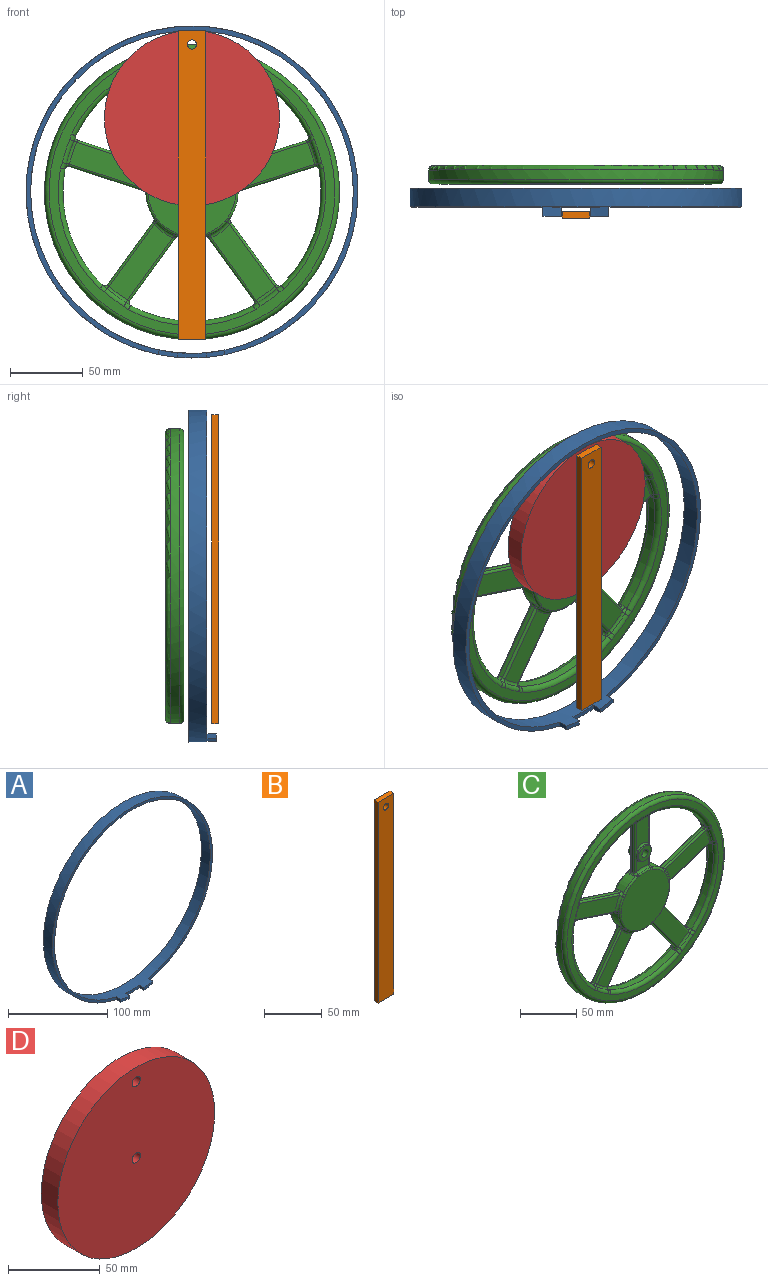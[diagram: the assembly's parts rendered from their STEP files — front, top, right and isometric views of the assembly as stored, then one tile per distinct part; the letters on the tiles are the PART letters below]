
ASSEMBLY  parts=4 mates=4
PART A: 11 faces, bbox 228.6x19.1x228.6 mm
  f0: plane 228.6x226.32mm, normal (0,-1,0), area 2103.2mm2, adj f2,f3,f6,f9
  f1: plane 20.07x3.63mm, normal (0,-1,0), area 63.8mm2, adj f2,f3,f5,f8
  f2: cylinder r=111.12mm len=222.25mm, axis (0,1,0), area 9030.5mm2, adj f0,f1,f4,f5,f6,f7,f8,f9
  f3: cylinder r=114.3mm len=228.6mm, axis (0,1,0), area 9283.8mm2, adj f0,f1,f4,f5,f6,f7,f8,f9
  f4: plane 228.6x228.6mm, normal (0,1,0), area 2248.5mm2, adj f2,f3
  f5: plane 6.35x3.19mm, normal (-1,0,0), area 20.2mm2, adj f1,f2,f3,f7
  f6: plane 6.35x3.24mm, normal (1,0,0), area 20.6mm2, adj f0,f2,f3,f7
  f7: plane 12.7x5.08mm, normal (0,-1,0), area 40.8mm2, adj f2,f3,f5,f6
  f8: plane 6.35x3.19mm, normal (1,0,0), area 20.2mm2, adj f1,f2,f3,f10
  f9: plane 6.35x3.24mm, normal (-1,0,0), area 20.6mm2, adj f0,f2,f3,f10
  f10: plane 12.7x5.08mm, normal (0,-1,0), area 40.8mm2, adj f2,f3,f8,f9
PART B: 7 faces, bbox 19.1x4.8x212.7 mm
  f0: plane 212.73x19.05mm, normal (0,-1,0), area 4020.7mm2, adj f1,f3,f4,f5,f6
  f1: plane 19.05x4.76mm, normal (0,0,-1), area 90.7mm2, adj f0,f2,f4,f5
  f2: plane 212.73x19.05mm, normal (0,1,0), area 4020.7mm2, adj f1,f3,f4,f5,f6
  f3: cylinder r=3.17mm len=6.35mm, axis (0,1,0), area 95mm2, adj f0,f2
  f4: plane 212.73x4.76mm, normal (1,0,0), area 1013.1mm2, adj f0,f1,f2,f6
  f5: plane 212.73x4.76mm, normal (-1,0,0), area 1013.1mm2, adj f0,f1,f2,f6
  f6: plane 19.05x4.76mm, normal (0,0,1), area 90.7mm2, adj f0,f2,f4,f5
PART C: 232 faces, bbox 219.9x12.7x219.9 mm
  f0: cylinder r=31.75mm len=19.11mm, axis (0,-1,0), area 174.7mm2, adj f72,f74,f76,f93,f95,f97,f205,f225
  f1: cylinder r=31.75mm len=20.1mm, axis (0,-1,0), area 174.7mm2, adj f96,f98,f100,f117,f119,f121,f197,f217
  f2: cylinder r=31.75mm len=19.11mm, axis (0,-1,0), area 174.7mm2, adj f120,f122,f124,f141,f143,f145,f192,f212
  f3: cylinder r=31.75mm len=16.26mm, axis (0,-1,0), area 174.7mm2, adj f33,f35,f37,f144,f146,f148,f200,f220
  f4: cylinder r=88.9mm len=80.24mm, axis (0,-1,0), area 554.9mm2, adj f113,f115,f116,f133,f134,f136,f166,f187
  f5: cylinder r=88.9mm len=84.37mm, axis (0,-1,0), area 554.9mm2, adj f89,f91,f92,f109,f110,f112,f158,f179
  f6: cylinder r=88.9mm len=80.24mm, axis (0,-1,0), area 554.9mm2, adj f65,f67,f68,f85,f86,f88,f150,f171
  f7: cylinder r=88.9mm len=68.25mm, axis (0,-1,0), area 554.9mm2, adj f29,f31,f32,f61,f62,f64,f155,f176
  f8: plane 15.88x12.36mm, normal (0,1,0), area 138.7mm2, adj f21,f22,f39,f46
  f9: plane 30.47x15.88mm, normal (0,-1,0), area 434.2mm2, adj f23,f24,f27,f51
  f10: plane 196.85x196.85mm, normal (0,1,0), area 3854.4mm2, adj f149,f150,f151,f152,f153,f154,f155,f156
  f11: cylinder r=101.6mm len=203.2mm, axis (0,-1,0), area 4053.7mm2, adj f169,f190
  f12: cylinder r=88.9mm len=68.25mm, axis (0,-1,0), area 554.9mm2, adj f25,f26,f28,f137,f139,f140,f163,f184
  f13: plane 196.85x196.85mm, normal (0,-1,0), area 3854.4mm2, adj f170,f171,f172,f173,f174,f175,f176,f177
  f14: plane 30.47x15.88mm, normal (0,1,0), area 434.2mm2, adj f21,f22,f30,f47
  f15: plane 53.74x3.18mm, normal (1,0,0), area 170.6mm2, adj f21,f24,f26,f35
  f16: plane 53.74x3.18mm, normal (-1,0,0), area 170.6mm2, adj f22,f23,f31,f38
  f17: plane 15.88x12.36mm, normal (0,-1,0), area 138.7mm2, adj f23,f24,f34,f50
  f18: plane 60.4x60.35mm, normal (0,1,0), area 2864.4mm2, adj f191,f192,f193,f194,f195,f196,f197,f198
  f19: plane 60.4x60.35mm, normal (0,-1,0), area 2864.4mm2, adj f211,f212,f213,f214,f215,f216,f217,f218
  f20: cylinder r=31.75mm len=16.26mm, axis (0,-1,0), area 174.7mm2, adj f36,f38,f40,f69,f71,f73,f208,f228
  f21: cylinder r=1.59mm len=54.2mm, axis (0,0,1), area 127.2mm2, adj f8,f14,f15,f28,f37,f45
  f22: cylinder r=1.59mm len=54.2mm, axis (0,0,-1), area 127.2mm2, adj f8,f14,f16,f32,f40,f48
  f23: cylinder r=1.59mm len=54.2mm, axis (0,0,-1), area 127.2mm2, adj f9,f16,f17,f29,f36,f49
  f24: cylinder r=1.59mm len=54.2mm, axis (0,0,1), area 127.2mm2, adj f9,f15,f17,f25,f33,f52
  f25: bspline ~4.96x4.83mm, area 11.7mm2, adj f12,f24,f26,f27,f182
  f26: cylinder r=2.36mm len=3.18mm, axis (0,-1,0), area 12.8mm2, adj f12,f15,f25,f28
  f27: torus R=86.54mm, axis (0,-1,0), area 43mm2, adj f9,f25,f29,f180
  f28: bspline ~4.96x4.83mm, area 11.7mm2, adj f12,f21,f26,f30,f161
  f29: bspline ~4.96x4.83mm, area 11.7mm2, adj f7,f23,f27,f31,f178
  f30: torus R=86.54mm, axis (0,1,0), area 43mm2, adj f14,f28,f32,f159
  f31: cylinder r=2.36mm len=3.18mm, axis (0,-1,0), area 12.8mm2, adj f7,f16,f29,f32
  f32: bspline ~4.96x4.83mm, area 11.7mm2, adj f7,f22,f30,f31,f157
  f33: bspline ~4.79x4.5mm, area 12.4mm2, adj f3,f24,f34,f35,f222
  f34: torus R=34.11mm, axis (0,-1,0), area 49.9mm2, adj f17,f33,f36,f224
  f35: cylinder r=2.36mm len=3.18mm, axis (0,-1,0), area 9.1mm2, adj f3,f15,f33,f37
  f36: bspline ~4.79x3.88mm, area 12.4mm2, adj f20,f23,f34,f38,f226
  f37: bspline ~4.79x4.5mm, area 12.4mm2, adj f3,f21,f35,f39,f202
  f38: cylinder r=2.36mm len=3.18mm, axis (0,-1,0), area 9.1mm2, adj f16,f20,f36,f40
  f39: torus R=34.11mm, axis (0,1,0), area 49.9mm2, adj f8,f37,f40,f204
  f40: bspline ~4.5x4.16mm, area 12.4mm2, adj f20,f22,f38,f39,f206
  f41: plane 15.88x15.88mm, normal (0,-1,0), area 148.4mm2, adj f42,f231
  f42: cylinder r=7.94mm len=15.88mm, axis (0,-1,0), area 79.2mm2, adj f41,f49,f50,f51,f52
  f43: cylinder r=7.94mm len=15.88mm, axis (0,-1,0), area 79.2mm2, adj f44,f45,f46,f47,f48
  f44: plane 15.88x15.88mm, normal (0,1,0), area 148.4mm2, adj f43,f231
  f45: bspline ~12.24x2.65mm, area 19.1mm2, adj f21,f43,f46,f47
  f46: torus R=9.53mm, axis (0,1,0), area 41.8mm2, adj f8,f43,f45,f48
  f47: torus R=9.53mm, axis (0,1,0), area 41.8mm2, adj f14,f43,f45,f48
  f48: bspline ~12.24x2.65mm, area 19.1mm2, adj f22,f43,f46,f47
  f49: bspline ~12.24x2.65mm, area 19.1mm2, adj f23,f42,f50,f51
  f50: torus R=9.53mm, axis (0,-1,0), area 41.8mm2, adj f17,f42,f49,f52
  f51: torus R=9.53mm, axis (0,-1,0), area 41.8mm2, adj f9,f42,f49,f52
  f52: bspline ~12.24x2.65mm, area 19.1mm2, adj f24,f42,f50,f51
  f53: plane 55.31x31.48mm, normal (0,1,0), area 835.3mm2, adj f57,f58,f66,f75
  f54: plane 51.11x16.61mm, normal (0.31,0,0.95), area 170.6mm2, adj f57,f60,f62,f71
  f55: plane 51.11x16.61mm, normal (-0.31,0,-0.95), area 170.6mm2, adj f58,f59,f67,f74
  f56: plane 55.31x31.48mm, normal (0,-1,0), area 835.3mm2, adj f59,f60,f63,f70
  f57: cylinder r=1.59mm len=52.04mm, axis (-0.95,0,0.31), area 133.1mm2, adj f53,f54,f64,f73
  f58: cylinder r=1.59mm len=52.04mm, axis (0.95,0,-0.31), area 133.1mm2, adj f53,f55,f68,f76
  f59: cylinder r=1.59mm len=52.04mm, axis (0.95,0,-0.31), area 133.1mm2, adj f55,f56,f65,f72
  f60: cylinder r=1.59mm len=52.04mm, axis (-0.95,0,0.31), area 133.1mm2, adj f54,f56,f61,f69
  f61: bspline ~4.96x4.17mm, area 11.7mm2, adj f7,f60,f62,f63,f174
  f62: cylinder r=2.36mm len=3.28mm, axis (0,-1,0), area 12.8mm2, adj f7,f54,f61,f64
  f63: torus R=86.54mm, axis (0,-1,0), area 43mm2, adj f56,f61,f65,f172
  f64: bspline ~4.96x4.83mm, area 11.7mm2, adj f7,f57,f62,f66,f153
  f65: bspline ~4.89x4.17mm, area 11.7mm2, adj f6,f59,f63,f67,f170
  f66: torus R=86.54mm, axis (0,1,0), area 43mm2, adj f53,f64,f68,f151
  f67: cylinder r=2.36mm len=3.18mm, axis (0,-1,0), area 12.8mm2, adj f6,f55,f65,f68
  f68: bspline ~4.89x4.83mm, area 11.7mm2, adj f6,f58,f66,f67,f149
  f69: bspline ~4.79x4.51mm, area 12.4mm2, adj f20,f60,f70,f71,f230
  f70: torus R=34.11mm, axis (0,-1,0), area 49.9mm2, adj f56,f69,f72,f229
  f71: cylinder r=2.36mm len=3.18mm, axis (0,-1,0), area 9.1mm2, adj f20,f54,f69,f73
  f72: bspline ~4.79x4.68mm, area 12.4mm2, adj f0,f59,f70,f74,f227
  f73: bspline ~4.79x4.51mm, area 12.4mm2, adj f20,f57,f71,f75,f210
  f74: cylinder r=2.36mm len=3.18mm, axis (0,-1,0), area 9.1mm2, adj f0,f55,f72,f76
  f75: torus R=34.11mm, axis (0,1,0), area 49.9mm2, adj f53,f73,f76,f209
  f76: bspline ~4.68x4.16mm, area 12.4mm2, adj f0,f58,f74,f75,f207
  f77: plane 52.21x43.99mm, normal (0,1,0), area 835.3mm2, adj f81,f82,f90,f99
  f78: plane 43.48x31.59mm, normal (-0.81,0,0.59), area 170.6mm2, adj f81,f84,f86,f95
  f79: plane 43.48x31.59mm, normal (0.81,0,-0.59), area 170.6mm2, adj f82,f83,f91,f98
  f80: plane 52.21x43.99mm, normal (0,-1,0), area 835.3mm2, adj f83,f84,f87,f94
  f81: cylinder r=1.59mm len=44.78mm, axis (-0.59,0,-0.81), area 133.1mm2, adj f77,f78,f88,f97
  f82: cylinder r=1.59mm len=44.78mm, axis (0.59,0,0.81), area 133.1mm2, adj f77,f79,f92,f100
  f83: cylinder r=1.59mm len=44.78mm, axis (0.59,0,0.81), area 133.1mm2, adj f79,f80,f89,f96
  f84: cylinder r=1.59mm len=44.78mm, axis (-0.59,0,-0.81), area 133.1mm2, adj f78,f80,f85,f93
  f85: bspline ~4.83x4.81mm, area 11.7mm2, adj f6,f84,f86,f87,f173
  f86: cylinder r=2.36mm len=3.55mm, axis (0,-1,0), area 12.8mm2, adj f6,f78,f85,f88
  f87: torus R=86.54mm, axis (0,-1,0), area 43mm2, adj f80,f85,f89,f175
  f88: bspline ~4.83x4.81mm, area 11.7mm2, adj f6,f81,f86,f90,f152
  f89: bspline ~4.83x4.34mm, area 11.7mm2, adj f5,f83,f87,f91,f177
  f90: torus R=86.54mm, axis (0,1,0), area 43mm2, adj f77,f88,f92,f154
  f91: cylinder r=2.36mm len=3.47mm, axis (0,-1,0), area 12.8mm2, adj f5,f79,f89,f92
  f92: bspline ~4.83x4.34mm, area 11.7mm2, adj f5,f82,f90,f91,f156
  f93: bspline ~4.97x4.79mm, area 12.4mm2, adj f0,f84,f94,f95,f223
  f94: torus R=34.11mm, axis (0,-1,0), area 49.9mm2, adj f80,f93,f96,f221
  f95: cylinder r=2.36mm len=3.18mm, axis (0,-1,0), area 9.1mm2, adj f0,f78,f93,f97
  f96: bspline ~4.94x4.16mm, area 12.4mm2, adj f1,f83,f94,f98,f219
  f97: bspline ~4.79x4.7mm, area 12.4mm2, adj f0,f81,f95,f99,f203
  f98: cylinder r=2.36mm len=3.18mm, axis (0,-1,0), area 9.1mm2, adj f1,f79,f96,f100
  f99: torus R=34.11mm, axis (0,1,0), area 49.9mm2, adj f77,f97,f100,f201
  f100: bspline ~4.94x4.16mm, area 12.4mm2, adj f1,f82,f98,f99,f199
  f101: plane 52.21x43.99mm, normal (0,1,0), area 835.3mm2, adj f105,f106,f114,f123
  f102: plane 43.48x31.59mm, normal (-0.81,0,-0.59), area 170.6mm2, adj f105,f108,f110,f119
  f103: plane 43.48x31.59mm, normal (0.81,0,0.59), area 170.6mm2, adj f106,f107,f115,f122
  f104: plane 52.21x43.99mm, normal (0,-1,0), area 835.3mm2, adj f107,f108,f111,f118
  f105: cylinder r=1.59mm len=44.78mm, axis (0.59,0,-0.81), area 133.1mm2, adj f101,f102,f112,f121
  f106: cylinder r=1.59mm len=44.78mm, axis (-0.59,0,0.81), area 133.1mm2, adj f101,f103,f116,f124
  f107: cylinder r=1.59mm len=44.78mm, axis (-0.59,0,0.81), area 133.1mm2, adj f103,f104,f113,f120
  f108: cylinder r=1.59mm len=44.78mm, axis (0.59,0,-0.81), area 133.1mm2, adj f102,f104,f109,f117
  f109: bspline ~4.83x4.34mm, area 11.7mm2, adj f5,f108,f110,f111,f181
  f110: cylinder r=2.36mm len=3.47mm, axis (0,-1,0), area 12.8mm2, adj f5,f102,f109,f112
  f111: torus R=86.54mm, axis (0,-1,0), area 43mm2, adj f104,f109,f113,f183
  f112: bspline ~4.83x4.34mm, area 11.7mm2, adj f5,f105,f110,f114,f160
  f113: bspline ~4.83x4.81mm, area 11.7mm2, adj f4,f107,f111,f115,f185
  f114: torus R=86.54mm, axis (0,1,0), area 43mm2, adj f101,f112,f116,f162
  f115: cylinder r=2.36mm len=3.55mm, axis (0,-1,0), area 12.8mm2, adj f4,f103,f113,f116
  f116: bspline ~4.83x4.81mm, area 11.7mm2, adj f4,f106,f114,f115,f164
  f117: bspline ~4.94x4.79mm, area 12.4mm2, adj f1,f108,f118,f119,f215
  f118: torus R=34.11mm, axis (0,-1,0), area 49.9mm2, adj f104,f117,f120,f213
  f119: cylinder r=2.36mm len=3.18mm, axis (0,-1,0), area 9.1mm2, adj f1,f102,f117,f121
  f120: bspline ~4.97x4.16mm, area 12.4mm2, adj f2,f107,f118,f122,f211
  f121: bspline ~4.79x4.64mm, area 12.4mm2, adj f1,f105,f119,f123,f195
  f122: cylinder r=2.36mm len=3.18mm, axis (0,-1,0), area 9.1mm2, adj f2,f103,f120,f124
  f123: torus R=34.11mm, axis (0,1,0), area 49.9mm2, adj f101,f121,f124,f193
  f124: bspline ~4.97x4.79mm, area 12.4mm2, adj f2,f106,f122,f123,f191
  f125: plane 55.31x31.48mm, normal (0,1,0), area 835.3mm2, adj f129,f130,f138,f147
  f126: plane 51.11x16.61mm, normal (0.31,0,-0.95), area 170.6mm2, adj f129,f132,f134,f143
  f127: plane 51.11x16.61mm, normal (-0.31,0,0.95), area 170.6mm2, adj f130,f131,f139,f146
  f128: plane 55.31x31.48mm, normal (0,-1,0), area 835.3mm2, adj f131,f132,f135,f142
  f129: cylinder r=1.59mm len=52.04mm, axis (0.95,0,0.31), area 133.1mm2, adj f125,f126,f136,f145
  f130: cylinder r=1.59mm len=52.04mm, axis (-0.95,0,-0.31), area 133.1mm2, adj f125,f127,f140,f148
  f131: cylinder r=1.59mm len=52.04mm, axis (-0.95,0,-0.31), area 133.1mm2, adj f127,f128,f137,f144
  f132: cylinder r=1.59mm len=52.04mm, axis (0.95,0,0.31), area 133.1mm2, adj f126,f128,f133,f141
  f133: bspline ~4.89x4.83mm, area 11.7mm2, adj f4,f132,f134,f135,f189
  f134: cylinder r=2.36mm len=3.18mm, axis (0,-1,0), area 12.8mm2, adj f4,f126,f133,f136
  f135: torus R=86.54mm, axis (0,-1,0), area 43mm2, adj f128,f133,f137,f188
  f136: bspline ~4.89x4.83mm, area 11.7mm2, adj f4,f129,f134,f138,f168
  f137: bspline ~4.96x4.83mm, area 11.7mm2, adj f12,f131,f135,f139,f186
  f138: torus R=86.54mm, axis (0,1,0), area 43mm2, adj f125,f136,f140,f167
  f139: cylinder r=2.36mm len=3.28mm, axis (0,-1,0), area 12.8mm2, adj f12,f127,f137,f140
  f140: bspline ~4.96x4.17mm, area 11.7mm2, adj f12,f130,f138,f139,f165
  f141: bspline ~4.79x4.68mm, area 12.4mm2, adj f2,f132,f142,f143,f214
  f142: torus R=34.11mm, axis (0,-1,0), area 49.9mm2, adj f128,f141,f144,f216
  f143: cylinder r=2.36mm len=3.18mm, axis (0,-1,0), area 9.1mm2, adj f2,f126,f141,f145
  f144: bspline ~4.79x4.51mm, area 12.4mm2, adj f3,f131,f142,f146,f218
  f145: bspline ~4.79x4.68mm, area 12.4mm2, adj f2,f129,f143,f147,f194
  f146: cylinder r=2.36mm len=3.18mm, axis (0,-1,0), area 9.1mm2, adj f3,f127,f144,f148
  f147: torus R=34.11mm, axis (0,1,0), area 49.9mm2, adj f125,f145,f148,f196
  f148: bspline ~4.51x4.16mm, area 12.4mm2, adj f3,f130,f146,f147,f198
  f149: bspline ~5.07x4.22mm, area 15.8mm2, adj f10,f68,f150,f151
  f150: torus R=92.08mm, axis (0,1,0), area 444.1mm2, adj f6,f10,f149,f152
  f151: torus R=91.55mm, axis (0,1,0), area 59.3mm2, adj f10,f66,f149,f153
  f152: bspline ~5.76x4.91mm, area 15.8mm2, adj f10,f88,f150,f154
  f153: bspline ~6.52x4.64mm, area 15.8mm2, adj f10,f64,f151,f155
  f154: torus R=91.55mm, axis (0,1,0), area 59.3mm2, adj f10,f90,f152,f156
  f155: torus R=92.08mm, axis (0,1,0), area 444.1mm2, adj f7,f10,f153,f157
  f156: bspline ~5.54x5.47mm, area 15.8mm2, adj f10,f92,f154,f158
  f157: bspline ~5.84x3.57mm, area 15.8mm2, adj f10,f32,f155,f159
  f158: torus R=92.08mm, axis (0,1,0), area 444.1mm2, adj f5,f10,f156,f160
  f159: torus R=91.55mm, axis (0,1,0), area 59.3mm2, adj f10,f30,f157,f161
  f160: bspline ~5.27x5.09mm, area 15.8mm2, adj f10,f112,f158,f162
  f161: bspline ~6.02x3.57mm, area 15.8mm2, adj f10,f28,f159,f163
  f162: torus R=91.55mm, axis (0,1,0), area 59.3mm2, adj f10,f114,f160,f164
  f163: torus R=92.08mm, axis (0,1,0), area 444.1mm2, adj f10,f12,f161,f165
  f164: bspline ~6.04x5.17mm, area 15.8mm2, adj f10,f116,f162,f166
  f165: bspline ~6.36x4.59mm, area 15.8mm2, adj f10,f140,f163,f167
  f166: torus R=92.08mm, axis (0,1,0), area 444.1mm2, adj f4,f10,f164,f168
  f167: torus R=91.55mm, axis (0,1,0), area 59.3mm2, adj f10,f138,f165,f168
  f168: bspline ~5.34x4.32mm, area 15.8mm2, adj f10,f136,f166,f167
  f169: torus R=98.42mm, axis (0,1,0), area 3147.6mm2, adj f10,f11
  f170: bspline ~5.07x4.22mm, area 15.8mm2, adj f13,f65,f171,f172
  f171: torus R=92.08mm, axis (0,-1,0), area 444.1mm2, adj f6,f13,f170,f173
  f172: torus R=91.55mm, axis (0,-1,0), area 59.3mm2, adj f13,f63,f170,f174
  f173: bspline ~6.39x5.37mm, area 15.8mm2, adj f13,f85,f171,f175
  f174: bspline ~6.52x4.64mm, area 15.8mm2, adj f13,f61,f172,f176
  f175: torus R=91.55mm, axis (0,-1,0), area 59.3mm2, adj f13,f87,f173,f177
  f176: torus R=92.08mm, axis (0,-1,0), area 444.1mm2, adj f7,f13,f174,f178
  f177: bspline ~5.54x5.47mm, area 15.8mm2, adj f13,f89,f175,f179
  f178: bspline ~5.84x3.57mm, area 15.8mm2, adj f13,f29,f176,f180
  f179: torus R=92.08mm, axis (0,-1,0), area 444.1mm2, adj f5,f13,f177,f181
  f180: torus R=91.55mm, axis (0,-1,0), area 59.3mm2, adj f13,f27,f178,f182
  f181: bspline ~5.63x5.57mm, area 15.8mm2, adj f13,f109,f179,f183
  f182: bspline ~6.02x3.57mm, area 15.8mm2, adj f13,f25,f180,f184
  f183: torus R=91.55mm, axis (0,-1,0), area 59.3mm2, adj f13,f111,f181,f185
  f184: torus R=92.08mm, axis (0,-1,0), area 444.1mm2, adj f12,f13,f182,f186
  f185: bspline ~6.04x5.17mm, area 15.8mm2, adj f13,f113,f183,f187
  f186: bspline ~6.36x4.59mm, area 15.8mm2, adj f13,f137,f184,f188
  f187: torus R=92.08mm, axis (0,-1,0), area 444.1mm2, adj f4,f13,f185,f189
  f188: torus R=91.55mm, axis (0,-1,0), area 59.3mm2, adj f13,f135,f186,f189
  f189: bspline ~5.34x4.32mm, area 15.8mm2, adj f13,f133,f187,f188
  f190: torus R=98.42mm, axis (0,-1,0), area 3147.6mm2, adj f11,f13
  f191: bspline ~3.84x3.45mm, area 5.1mm2, adj f18,f124,f192,f193
  f192: torus R=30.16mm, axis (0,1,0), area 50.1mm2, adj f2,f18,f191,f194
  f193: torus R=30.24mm, axis (0,-1,0), area 31.9mm2, adj f18,f123,f191,f195
  f194: bspline ~3.5x1.81mm, area 5.1mm2, adj f18,f145,f192,f196
  f195: bspline ~3.78x2.7mm, area 5.1mm2, adj f18,f121,f193,f197
  f196: torus R=30.24mm, axis (0,-1,0), area 31.9mm2, adj f18,f147,f194,f198
  f197: torus R=30.16mm, axis (0,1,0), area 50.1mm2, adj f1,f18,f195,f199
  f198: bspline ~3.79x3.34mm, area 5.1mm2, adj f18,f148,f196,f200
  f199: bspline ~3.97x2.78mm, area 5.1mm2, adj f18,f100,f197,f201
  f200: torus R=30.16mm, axis (0,1,0), area 50.1mm2, adj f3,f18,f198,f202
  f201: torus R=30.24mm, axis (0,-1,0), area 31.9mm2, adj f18,f99,f199,f203
  f202: bspline ~3.58x2.47mm, area 5.1mm2, adj f18,f37,f200,f204
  f203: bspline ~3.69x3.33mm, area 5.1mm2, adj f18,f97,f201,f205
  f204: torus R=30.24mm, axis (0,-1,0), area 31.9mm2, adj f18,f39,f202,f206
  f205: torus R=30.16mm, axis (0,1,0), area 50.1mm2, adj f0,f18,f203,f207
  f206: bspline ~3.76x2.51mm, area 5.1mm2, adj f18,f40,f204,f208
  f207: bspline ~3.71x1.83mm, area 5.1mm2, adj f18,f76,f205,f209
  f208: torus R=30.16mm, axis (0,1,0), area 50.1mm2, adj f18,f20,f206,f210
  f209: torus R=30.24mm, axis (0,-1,0), area 31.9mm2, adj f18,f75,f207,f210
  f210: bspline ~3.63x3.24mm, area 5.1mm2, adj f18,f73,f208,f209
  f211: bspline ~4.33x3.89mm, area 5.1mm2, adj f19,f120,f212,f213
  f212: torus R=30.16mm, axis (0,-1,0), area 50.1mm2, adj f2,f19,f211,f214
  f213: torus R=30.24mm, axis (0,1,0), area 31.9mm2, adj f19,f118,f211,f215
  f214: bspline ~4.16x1.99mm, area 5.1mm2, adj f19,f141,f212,f216
  f215: bspline ~4.38x3.02mm, area 5.1mm2, adj f19,f117,f213,f217
  f216: torus R=30.24mm, axis (0,1,0), area 31.9mm2, adj f19,f142,f214,f218
  f217: torus R=30.16mm, axis (0,-1,0), area 50.1mm2, adj f1,f19,f215,f219
  f218: bspline ~3.86x3.39mm, area 5.1mm2, adj f19,f144,f216,f220
  f219: bspline ~4.57x3.1mm, area 5.1mm2, adj f19,f96,f217,f221
  f220: torus R=30.16mm, axis (0,-1,0), area 50.1mm2, adj f3,f19,f218,f222
  f221: torus R=30.24mm, axis (0,1,0), area 31.9mm2, adj f19,f94,f219,f223
  f222: bspline ~4.09x2.6mm, area 5.1mm2, adj f19,f33,f220,f224
  f223: bspline ~4.18x3.76mm, area 5.1mm2, adj f19,f93,f221,f225
  f224: torus R=30.24mm, axis (0,1,0), area 31.9mm2, adj f19,f34,f222,f226
  f225: torus R=30.16mm, axis (0,-1,0), area 50.1mm2, adj f0,f19,f223,f227
  f226: bspline ~4.27x2.64mm, area 5.1mm2, adj f19,f36,f224,f228
  f227: bspline ~4.37x2.01mm, area 5.1mm2, adj f19,f72,f225,f229
  f228: torus R=30.16mm, axis (0,-1,0), area 50.1mm2, adj f19,f20,f226,f230
  f229: torus R=30.24mm, axis (0,1,0), area 31.9mm2, adj f19,f70,f227,f230
  f230: bspline ~4.13x3.57mm, area 5.1mm2, adj f19,f69,f228,f229
  f231: cylinder r=3.97mm len=12.7mm, axis (0,-1,0), area 316.7mm2, adj f41,f44
PART D: 5 faces, bbox 120.7x12.7x120.7 mm
  f0: plane 120.65x120.65mm, normal (0,-1,0), area 11369.2mm2, adj f1,f2,f3
  f1: cylinder r=3.17mm len=12.7mm, axis (0,1,0), area 253.4mm2, adj f0,f4
  f2: cylinder r=3.17mm len=12.7mm, axis (0,1,0), area 253.4mm2, adj f0,f4
  f3: cylinder r=60.32mm len=120.65mm, axis (0,1,0), area 4813.7mm2, adj f0,f4
  f4: plane 120.65x120.65mm, normal (0,1,0), area 11369.2mm2, adj f1,f2,f3
PLACE A at identity fixed
PLACE B at identity
PLACE C rot(axis=(0,1,0),0deg) t=(0,0,0)mm
PLACE D rot(axis=(0,-1,0),0deg) t=(0.05,0,0)mm
MATE parallel B.f4 <-> A.f5  axis (1,0,0) through (9.53,-21.43,4.76)mm
MATE revolute B.f3 <-> D.f2  axis (0,1,0) through (0,-19.05,101.6)mm
MATE revolute C.f0 <-> A.f2  axis (0,-1,0) through (0,0,0)mm
MATE revolute C.f42 <-> D.f3  axis (0,-1,0) through (0.03,0,50.8)mm
